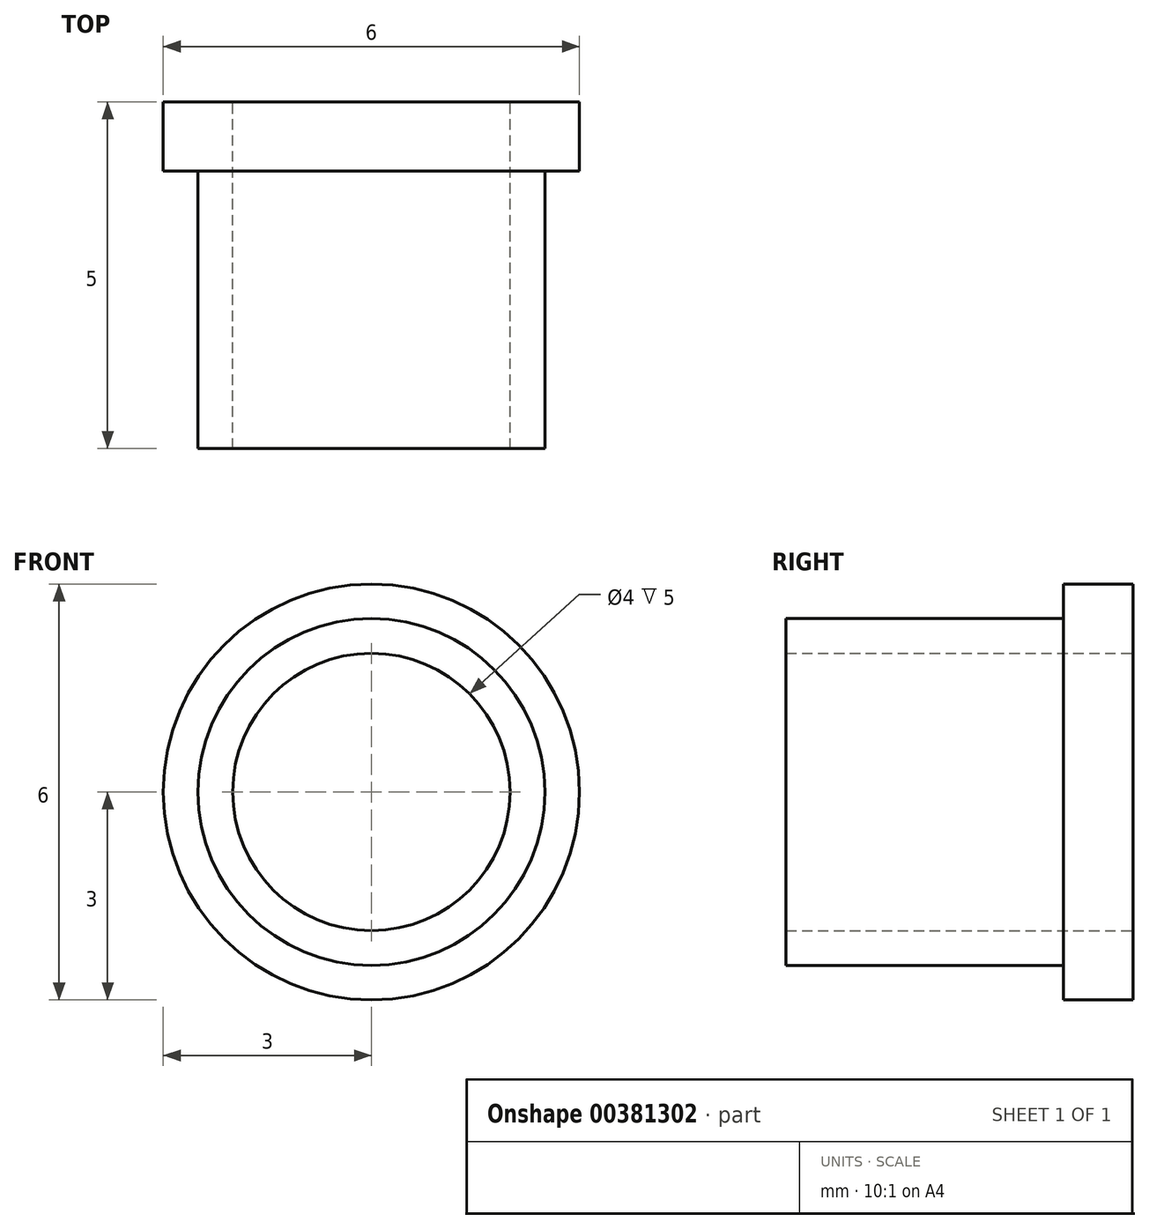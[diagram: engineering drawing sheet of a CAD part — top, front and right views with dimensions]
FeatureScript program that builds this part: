
annotation { "Feature Type Name" : "Feature", "Feature Type Description" : "" }
export const myFeature = defineFeature(function(context is Context, id is Id, definition is map)
    precondition{}
    {
        {
            var Q0;
            Q0=qCreatedBy(makeId("Top.planeOp"),FACE);
            var sketch = newSketch(context, id + "F0", { "sketchPlane" : qUnion([Q0])});
            skLineSegment(sketch, "E0", {"start": v(2, 0) * mm, "end": v(2, 5) * mm});
            skLineSegment(sketch, "E1", {"start": v(2, 5) * mm, "end": v(3, 5) * mm});
            skLineSegment(sketch, "E2", {"start": v(3, 5) * mm, "end": v(3, 4) * mm});
            skLineSegment(sketch, "E3", {"start": v(3, 4) * mm, "end": v(2.5, 4) * mm});
            skLineSegment(sketch, "E4", {"start": v(2.5, 4) * mm, "end": v(2.5, 0) * mm});
            skLineSegment(sketch, "E5", {"start": v(2.5, 0) * mm, "end": v(2, 0) * mm});
            skLineSegment(sketch, "E6", {"start": v(0, 44.42) * mm, "end": v(0, 0) * mm, "construction": true});
            skSolve(sketch);
        }
        {
            var Q0;
            Q0=makeQuery(id+"F0.imprint","IMPRINT",FACE,{"disambiguationData":[TD([[makeQuery(id+"F0.imprint","IMPRINT",EDGE,{"derivedFrom":sQuery(id+"F0.wireOp",EDGE,"E0")}),-1.0]])]});
            var Q1;
            Q1=sQuery(id+"F0.wireOp",EDGE,"E6");
            revolve(context, id + "F1", {"entities" : qUnion([Q0]), "axis" : qUnion([Q1]), "revolveType" : RevolveType.FULL});
        }
    });
